# Revit family: T-Abzweigstück_horizontal_ Russia
name_source: partatom
category: Generic Models
revit_build: Autodesk Revit 2015 (Build: 20140606_1530(x64)
units: mm (PartAtom-declared; Revit-internal decimal feet)

## types (7) — shared parameters
Manufacturer = OBO Bettermann
Material = Stainless Steel
URL = http://www.obo-bettermann.com

## per-type parameters (varying)
| type | A | GTIN | L | Manufacturer Art.No. | c |
| RT 610 FS RU | 98 mm  [stored 0.321522 ft] | 4012196606184 | 432 mm | 6043302 | 106 mm  [stored 0.347769 ft] |
| RT 615 FS RU | 148 mm  [stored 0.485564 ft] | 4012196649358 | 482 mm | 6043303 | 106 mm  [stored 0.347769 ft] |
| RT 620 FS RU | 198 mm  [stored 0.649606 ft] | 4012196606191 | 603 mm | 6043304 | 141 mm |
| RT 630 FS RU | 298 mm  [stored 0.97769 ft] | 4012196606177 | 703 mm | 6043306 | 141 mm |
| RT 640 FS RU | 398 mm  [stored 1.30577 ft] | 4012196626038 | 803 mm | 6043308 | 141 mm |
| RT 650 FS RU | 498 mm  [stored 1.63386 ft] | 4012196626045 | 903 mm | 6043310 | 141 mm |
| RT 660 FS RU | 598 mm  [stored 1.96194 ft] | 4012196626076 | 1003 mm | 6043312 | 141 mm |

note: column(s) folded — value = type name in every type: Article Type

note: [stored X ft] marks values corroborated as IEEE doubles in the binary element streams (Revit-internal decimal feet)

## geometry (parser evidence)
native form markers: Sweep x2
no freeform markers — native parametric forms only
